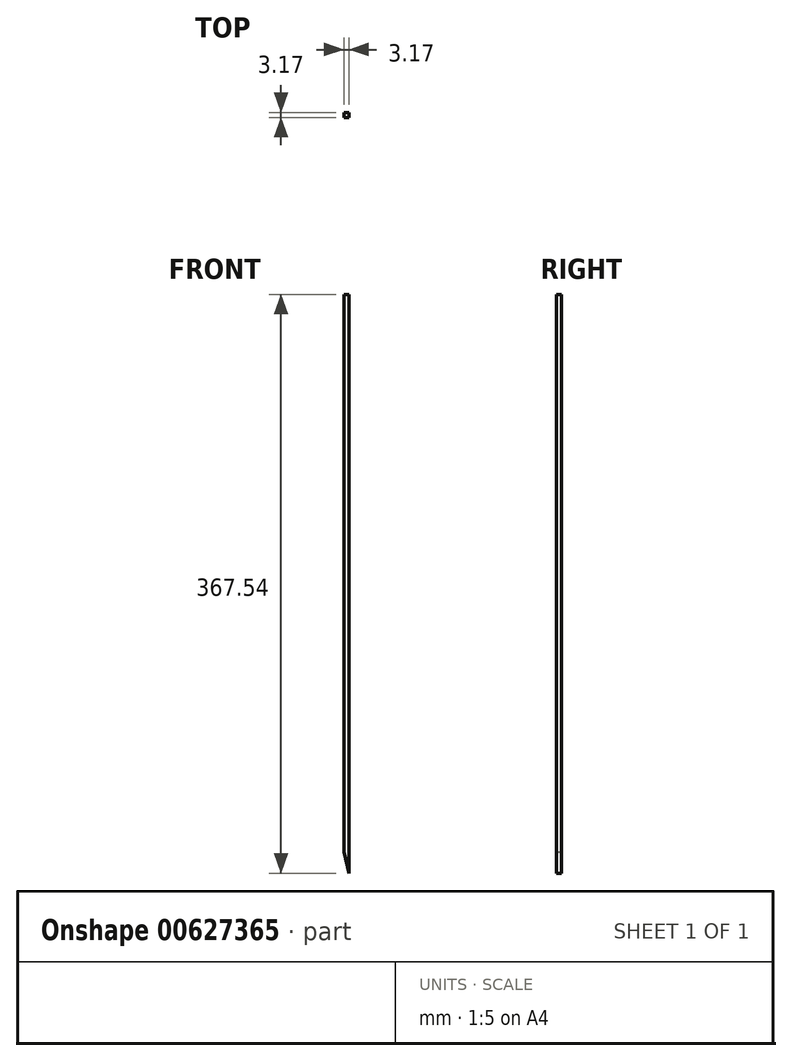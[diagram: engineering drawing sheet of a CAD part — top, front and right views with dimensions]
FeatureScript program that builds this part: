
annotation { "Feature Type Name" : "Feature", "Feature Type Description" : "" }
export const myFeature = defineFeature(function(context is Context, id is Id, definition is map)
    precondition{}
    {
        {
            var Q0;
            Q0=qCreatedBy(makeId("Front.planeOp"),FACE);
            var sketch = newSketch(context, id + "F0", { "sketchPlane" : qUnion([Q0])});
            skLineSegment(sketch, "E0", {"start": v(-13.35, 7.55) * mm, "end": v(-13.35, 375.1) * mm});
            skLineSegment(sketch, "E1", {"start": v(-13.35, 375.1) * mm, "end": v(-16.52, 375.1) * mm});
            skLineSegment(sketch, "E2", {"start": v(-16.52, 375.1) * mm, "end": v(-16.52, 21.18) * mm});
            skLineSegment(sketch, "E3", {"start": v(-16.52, 21.18) * mm, "end": v(-13.35, 7.55) * mm});
            skSolve(sketch);
        }
        {
            var Q0;
            Q0=makeQuery(id+"F0.imprint","IMPRINT",FACE,{"disambiguationData":[TD([[makeQuery(id+"F0.imprint","IMPRINT",EDGE,{"derivedFrom":sQuery(id+"F0.wireOp",EDGE,"E0")}),1.0]])]});
            extrude(context, id + "F1", {"entities" : qUnion([Q0]), "depth" : 3.17 * mm, "offsetDistance" : 25.4 * mm});
        }
    });
